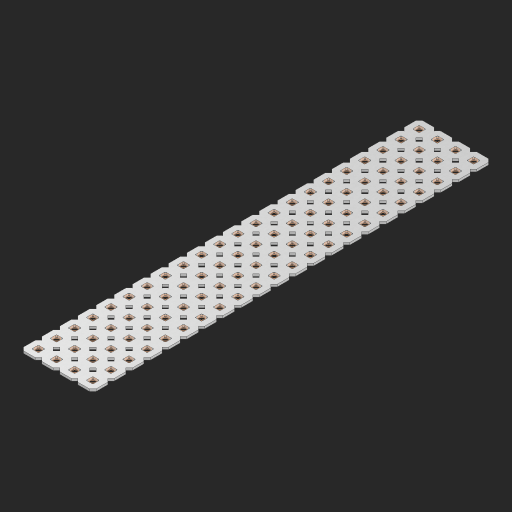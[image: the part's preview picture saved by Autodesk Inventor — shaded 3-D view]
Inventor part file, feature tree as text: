
AUTODESK INVENTOR PART (.ipt)
format: ipt  version: 2023 (Build 270158000, 158)  size: 1,295,872 bytes
history: native  units: in
note: dims shown in document units (in); Inventor stores cm internally (conversion verified against a paired STEP export)
features: other x89, extrude x87, sketch x2, pattern_linear x1
ambient origin geometry x8: Origin, YZ Plane, XZ Plane, XY Plane, X Axis, Y Axis, Z Axis, Center Point
bodies: Solid1 (feature_tree), Body (feature_tree)
feature tree (179):
  pattern_linear  "Rectangular Pattern1"  Spacing1=0.09in  [1 undecoded]
  sketch  "Sketch1"  dims[d1=0.5in]
  sketch  "Sketch2"  dims[d2=0.182in d3=0.09in d4=0.09in d5=0.09in d6=0.09in d7=0.09in d8=0.09in d9=0.09in d10=0.09in d11=0.02in d13=0.0in d14=0.172in d15=0.0625in d16=0.0in d19=0.5in d22=0.5in]
  other  "Srf1"
  other  "Srf126"
  other  "Srf127"
  other  "Srf128"
  other  "Srf129"
  other  "Srf130"
  other  "Srf131"
  other  "Srf250"
  other  "Srf251"
  other  "Srf252"
  other  "Srf253"
  other  "Srf254"
  other  "Srf255"
  other  "Srf256"
  other  "Srf257"
  other  "Srf258"
  other  "Srf259"
  other  "Srf260"
  other  "Srf261"
  other  "Srf262"
  other  "Srf263"
  other  "Srf264"
  other  "Srf268"
  other  "Srf269"
  other  "Srf270"
  other  "Srf271"
  other  "Srf272"
  other  "Srf273"
  other  "Srf274"
  other  "Srf275"
  other  "Srf276"
  other  "Srf277"
  other  "Srf278"
  other  "Srf279"
  other  "Srf280"
  other  "Srf281"
  other  "Srf282"
  other  "Srf283"
  other  "Srf284"
  other  "Srf285"
  other  "Srf286"
  other  "Srf287"
  other  "Srf288"
  other  "Srf289"
  other  "Srf293"
  other  "Srf294"
  other  "Srf295"
  other  "Srf296"
  other  "Srf297"
  other  "Srf298"
  other  "Srf299"
  other  "Srf300"
  other  "Srf301"
  other  "Srf302"
  other  "Srf303"
  other  "Srf304"
  other  "Srf305"
  other  "Srf306"
  other  "Srf307"
  other  "Srf308"
  other  "Srf309"
  other  "Srf310"
  other  "Srf311"
  other  "Srf312"
  other  "Srf313"
  other  "Srf314"
  other  "Srf318"
  other  "Srf319"
  other  "Srf320"
  other  "Srf321"
  other  "Srf322"
  other  "Srf323"
  other  "Srf324"
  other  "Srf325"
  other  "Srf326"
  other  "Srf327"
  other  "Srf328"
  other  "Srf329"
  other  "Srf330"
  other  "Srf331"
  other  "Srf332"
  other  "Srf333"
  other  "Srf334"
  other  "Srf335"
  other  "Srf336"
  other  "Srf337"
  other  "Srf338"
  other  "Srf339"
  other  "Circle"
  extrude  "ExtrusionSrf126"  Depth=0.09in
  extrude  "ExtrusionSrf127"  Depth=0.09in
  extrude  "ExtrusionSrf128"  Depth=0.09in
  extrude  "ExtrusionSrf129"  Depth=0.09in
  extrude  "ExtrusionSrf130"  Depth=0.09in
  extrude  "ExtrusionSrf131"  Depth=0.09in
  extrude  "ExtrusionSrf250"  Depth=0.09in
  extrude  "ExtrusionSrf251"  Depth=0.02in
  extrude  "ExtrusionSrf252"  TaperAngle=0.0deg  [1 undecoded]
  extrude  "ExtrusionSrf253"  Depth=0.5in
  extrude  "ExtrusionSrf254"  Depth=0.0625in TaperAngle=0.0deg
  extrude  "ExtrusionSrf255"  Depth=0.5in
  extrude  "ExtrusionSrf256"  Depth=0.5in
  extrude  "ExtrusionSrf257"  [1 undecoded]
  extrude  "ExtrusionSrf258"  [1 undecoded]
  extrude  "ExtrusionSrf259"  [1 undecoded]
  extrude  "ExtrusionSrf260"  [1 undecoded]
  extrude  "ExtrusionSrf261"  [1 undecoded]
  extrude  "ExtrusionSrf262"  [1 undecoded]
  extrude  "ExtrusionSrf263"  [1 undecoded]
  extrude  "ExtrusionSrf264"  [1 undecoded]
  extrude  "ExtrusionSrf268"  [1 undecoded]
  extrude  "ExtrusionSrf269"  [1 undecoded]
  extrude  "ExtrusionSrf270"  [1 undecoded]
  extrude  "ExtrusionSrf271"  [1 undecoded]
  extrude  "ExtrusionSrf272"  [1 undecoded]
  extrude  "ExtrusionSrf273"  [1 undecoded]
  extrude  "ExtrusionSrf274"  [1 undecoded]
  extrude  "ExtrusionSrf275"  [1 undecoded]
  extrude  "ExtrusionSrf276"  [1 undecoded]
  extrude  "ExtrusionSrf277"  [1 undecoded]
  extrude  "ExtrusionSrf278"  [1 undecoded]
  extrude  "ExtrusionSrf279"  [1 undecoded]
  extrude  "ExtrusionSrf280"  [1 undecoded]
  extrude  "ExtrusionSrf281"  [1 undecoded]
  extrude  "ExtrusionSrf282"  [1 undecoded]
  extrude  "ExtrusionSrf283"  [1 undecoded]
  extrude  "ExtrusionSrf284"  [1 undecoded]
  extrude  "ExtrusionSrf285"  [1 undecoded]
  extrude  "ExtrusionSrf286"  [1 undecoded]
  extrude  "ExtrusionSrf287"  [1 undecoded]
  extrude  "ExtrusionSrf288"  [1 undecoded]
  extrude  "ExtrusionSrf289"  [1 undecoded]
  extrude  "ExtrusionSrf293"  [1 undecoded]
  extrude  "ExtrusionSrf294"  [1 undecoded]
  extrude  "ExtrusionSrf295"  [1 undecoded]
  extrude  "ExtrusionSrf296"  [1 undecoded]
  extrude  "ExtrusionSrf297"  [1 undecoded]
  extrude  "ExtrusionSrf298"  [1 undecoded]
  extrude  "ExtrusionSrf299"  [1 undecoded]
  extrude  "ExtrusionSrf300"  [1 undecoded]
  extrude  "ExtrusionSrf301"  [1 undecoded]
  extrude  "ExtrusionSrf302"  [1 undecoded]
  extrude  "ExtrusionSrf303"  [1 undecoded]
  extrude  "ExtrusionSrf304"  [1 undecoded]
  extrude  "ExtrusionSrf305"  [1 undecoded]
  extrude  "ExtrusionSrf306"  [1 undecoded]
  extrude  "ExtrusionSrf307"  [1 undecoded]
  extrude  "ExtrusionSrf308"  [1 undecoded]
  extrude  "ExtrusionSrf309"  [1 undecoded]
  extrude  "ExtrusionSrf310"  [1 undecoded]
  extrude  "ExtrusionSrf311"  [1 undecoded]
  extrude  "ExtrusionSrf312"  [1 undecoded]
  extrude  "ExtrusionSrf313"  [1 undecoded]
  extrude  "ExtrusionSrf314"  [1 undecoded]
  extrude  "ExtrusionSrf318"  [1 undecoded]
  extrude  "ExtrusionSrf319"  [1 undecoded]
  extrude  "ExtrusionSrf320"  [1 undecoded]
  extrude  "ExtrusionSrf321"  [1 undecoded]
  extrude  "ExtrusionSrf322"  [1 undecoded]
  extrude  "ExtrusionSrf323"  [1 undecoded]
  extrude  "ExtrusionSrf324"  [1 undecoded]
  extrude  "ExtrusionSrf325"  [1 undecoded]
  extrude  "ExtrusionSrf326"  [1 undecoded]
  extrude  "ExtrusionSrf327"  [1 undecoded]
  extrude  "ExtrusionSrf328"  [1 undecoded]
  extrude  "ExtrusionSrf329"  [1 undecoded]
  extrude  "ExtrusionSrf330"  [1 undecoded]
  extrude  "ExtrusionSrf331"  [1 undecoded]
  extrude  "ExtrusionSrf332"  [1 undecoded]
  extrude  "ExtrusionSrf333"  [1 undecoded]
  extrude  "ExtrusionSrf334"  [1 undecoded]
  extrude  "ExtrusionSrf335"  [1 undecoded]
  extrude  "ExtrusionSrf336"  [1 undecoded]
  extrude  "ExtrusionSrf337"  [1 undecoded]
  extrude  "ExtrusionSrf338"  [1 undecoded]
  extrude  "ExtrusionSrf339"  [1 undecoded]
note: 76 required parameter values undecoded (feature->parameter linkage not recoverable at this tier; creation-order binding heuristic only, values carry confidence <= 0.55)
